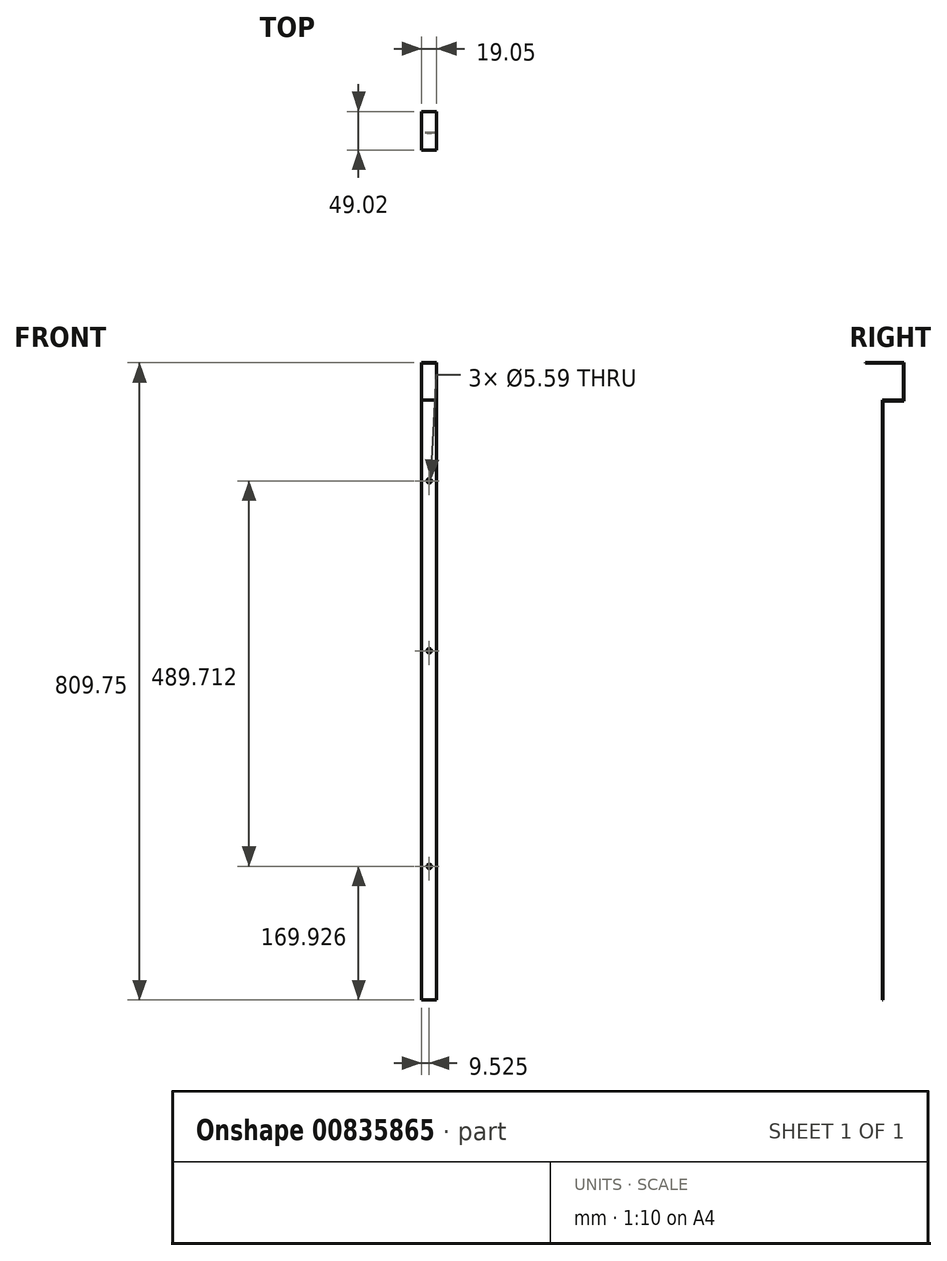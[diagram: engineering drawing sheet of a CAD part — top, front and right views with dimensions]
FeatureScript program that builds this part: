
annotation { "Feature Type Name" : "Feature", "Feature Type Description" : "" }
export const myFeature = defineFeature(function(context is Context, id is Id, definition is map)
    precondition{}
    {
        {
            var Q0;
            Q0=qCreatedBy(makeId("Right.planeOp"),FACE);
            var sketch = newSketch(context, id + "F0", { "sketchPlane" : qUnion([Q0])});
            skLineSegment(sketch, "E0", {"start": v(0, 0) * mm, "end": v(48.26, 0) * mm});
            skLineSegment(sketch, "E1", {"start": v(48.26, 0) * mm, "end": v(48.26, -46.99) * mm});
            skLineSegment(sketch, "E2", {"start": v(48.26, -46.99) * mm, "end": v(21.6, -47) * mm});
            skLineSegment(sketch, "E3", {"start": v(21.6, -47) * mm, "end": v(21.6, -809) * mm});
            skLineSegment(sketch, "E4", {"start": v(21.6, -809) * mm, "end": v(22.35, -809) * mm});
            skLineSegment(sketch, "E5", {"start": v(22.35, -809) * mm, "end": v(22.35, -47.75) * mm});
            skLineSegment(sketch, "E6", {"start": v(22.35, -47.75) * mm, "end": v(49.02, -47.75) * mm});
            skLineSegment(sketch, "E7", {"start": v(49.02, -47.75) * mm, "end": v(49.02, 0.76) * mm});
            skLineSegment(sketch, "E8", {"start": v(49.02, 0.76) * mm, "end": v(0, 0.76) * mm});
            skLineSegment(sketch, "E9", {"start": v(0, 0.76) * mm, "end": v(0, 0) * mm});
            skPoint(sketch, "E10", {"position": v(49.02, 0.76) * mm});
            skSolve(sketch);
        }
        {
            var Q0;
            Q0 = qSketchRegion(id + "F0", true);
            extrude(context, id + "F1", {"entities" : qUnion([Q0]), "depth" : 19.05 * mm, "offsetDistance" : 25.4 * mm});
        }
        {
            var Q0;
            Q0=makeQuery(id+"F1.opExtrude","SWEPT_FACE",FACE,{"disambiguationData":[OSD([sQuery(id+"F0.wireOp",EDGE,"E5")])]});
            var sketch = newSketch(context, id + "F2", { "sketchPlane" : qUnion([Q0])});
            skCircle(sketch, "E11", {"center": v(-9.52, -149.35) * mm, "radius": 2.8 * mm});
            skLineSegment(sketch, "E12", {"start": v(-19.05, -94) * mm, "end": v(0, -94) * mm});
            skPoint(sketch, "E13", {"position": v(-9.53, -94) * mm});
            skCircle(sketch, "E14", {"center": v(-9.52, -365.25) * mm, "radius": 2.8 * mm});
            skCircle(sketch, "E15", {"center": v(-9.52, -639.06) * mm, "radius": 2.8 * mm});
            skSolve(sketch);
        }
        {
            var Q0;
            Q0 = qSketchRegion(id + "F2", true);
            extrude(context, id + "F3", {"entities" : qUnion([Q0]), "operationType" : NewBodyOperationType.REMOVE, "oppositeDirection" : true, "depth" : 25.4 * mm, "offsetDistance" : 25.4 * mm});
        }
    });
